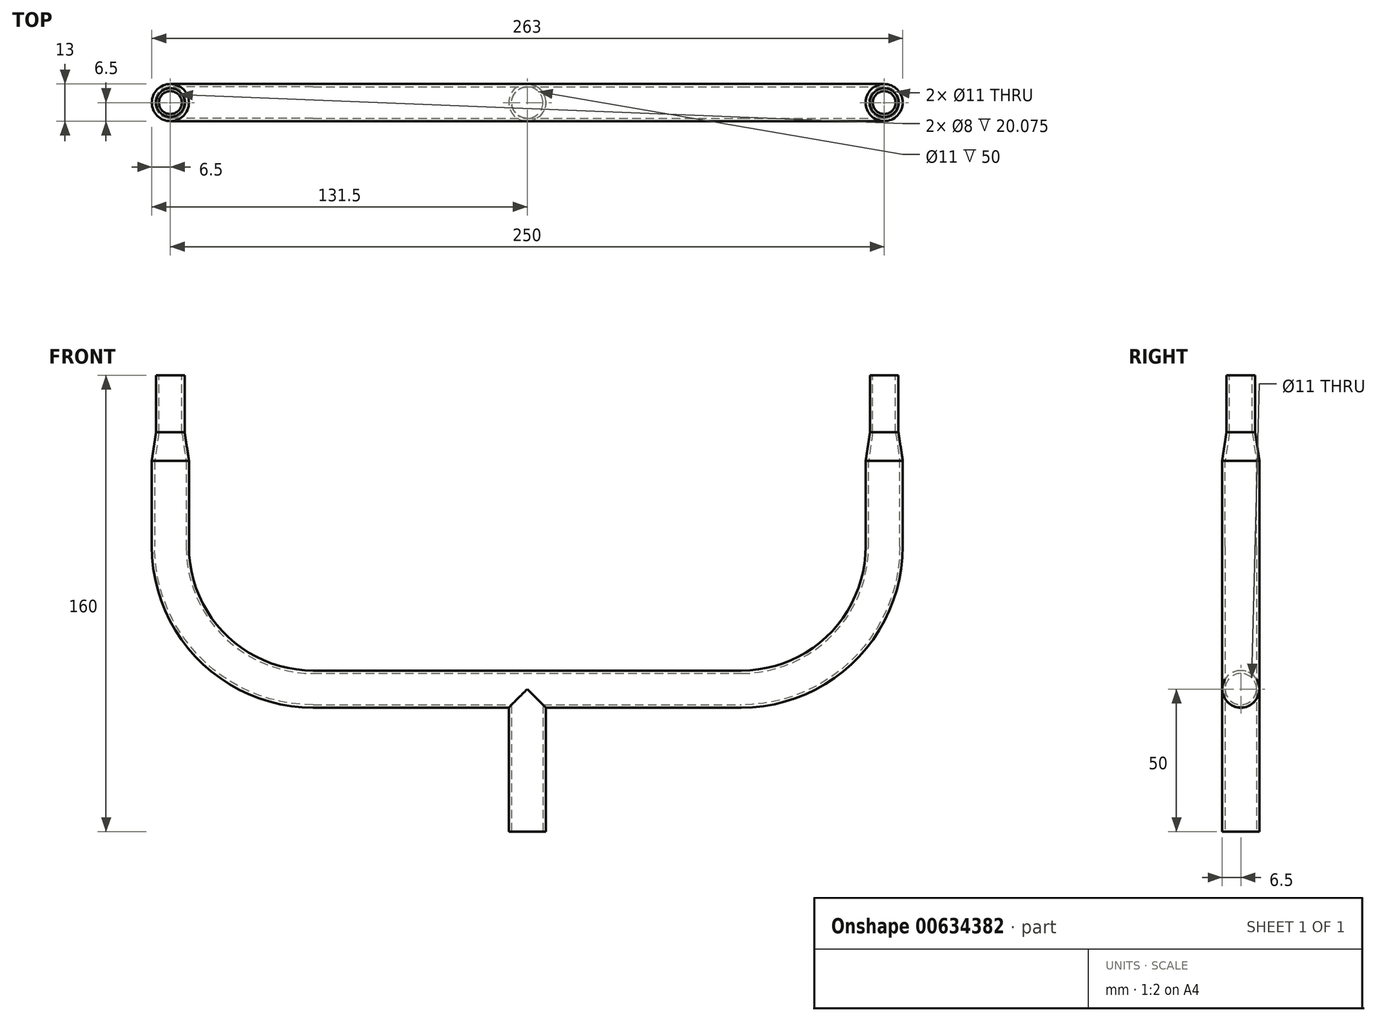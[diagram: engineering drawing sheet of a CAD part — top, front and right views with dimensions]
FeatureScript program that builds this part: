
annotation { "Feature Type Name" : "Feature", "Feature Type Description" : "" }
export const myFeature = defineFeature(function(context is Context, id is Id, definition is map)
    precondition{}
    {
        {
            var Q0;
            Q0=qCreatedBy(makeId("Front.planeOp"),FACE);
            var sketch = newSketch(context, id + "F0", { "sketchPlane" : qUnion([Q0])});
            skLineSegment(sketch, "E0", {"start": v(-75, 50) * mm, "end": v(75, 50) * mm});
            skArc(sketch, "E1", {"start": v(-75, 50) * mm, "mid": v(-110.36, 64.64) * mm, "end": v(-125, 100) * mm});
            skArc(sketch, "E2", {"start": v(75, 50) * mm, "mid": v(110.36, 64.64) * mm, "end": v(125, 100) * mm});
            skLineSegment(sketch, "E3", {"start": v(-125, 100) * mm, "end": v(-125, 120) * mm});
            skLineSegment(sketch, "E4", {"start": v(125, 100) * mm, "end": v(125, 120) * mm});
            skSolve(sketch);
        }
        {
            var Q0;
            Q0=qCreatedBy(makeId("Top.planeOp"),FACE);
            var Q1;
            Q1=sQuery(id+"F0.wireOp",VERTEX,"E3.end");
            cPlane(context, id + "F1", {"entities" : qUnion([Q0, Q1]), "cplaneType" : CPlaneType.PLANE_POINT, "offset" : 100 * mm, "width" : 150 * mm, "height" : 150 * mm});
        }
        {
            var Q0;
            Q0=qCreatedBy(id+"F1.planeOp",FACE);
            var sketch = newSketch(context, id + "F2", { "sketchPlane" : qUnion([Q0])});
            skCircle(sketch, "E5", {"center": v(-125, 0) * mm, "radius": 6.5 * mm});
            skCircle(sketch, "E6.0", {"center": v(-125, 0) * mm, "radius": 5.5 * mm});
            skSolve(sketch);
        }
        {
            var Q0;
            Q0=makeQuery(id+"F2.imprint","IMPRINT",FACE,{"disambiguationData":[TD([[makeQuery(id+"F2.imprint","IMPRINT",EDGE,{"derivedFrom":sQuery(id+"F2.wireOp",EDGE,"E5")}),1.0]])]});
            var Q1;
            Q1=qConstructionFilter(qBodyType(qCreatedBy(id+"F0",EDGE),BodyType.WIRE),ConstructionObject.NO);
            sweep(context, id + "F3", {"profiles" : qUnion([Q0]), "path" : qUnion([Q1])});
        }
        {
            var Q0;
            Q0=qCreatedBy(makeId("Top.planeOp"),FACE);
            var sketch = newSketch(context, id + "F4", { "sketchPlane" : qUnion([Q0])});
            skCircle(sketch, "E7", {"center": v(0, 0) * mm, "radius": 5.5 * mm});
            skSolve(sketch);
        }
        {
            var Q0;
            Q0=qSketchRegion(id+"F4",true);
            extrude(context, id + "F5", {"entities" : qUnion([Q0]), "operationType" : NewBodyOperationType.REMOVE, "depth" : 50 * mm});
        }
        {
            var Q0;
            Q0=qCreatedBy(makeId("Top.planeOp"),FACE);
            var sketch = newSketch(context, id + "F6", { "sketchPlane" : qUnion([Q0])});
            skCircle(sketch, "E8", {"center": v(0, 0) * mm, "radius": 6.5 * mm});
            skCircle(sketch, "E9", {"center": v(0, 0) * mm, "radius": 5.5 * mm});
            skSolve(sketch);
        }
        {
            var Q0;
            Q0=makeQuery(id+"F6.imprint","IMPRINT",FACE,{"disambiguationData":[TD([[makeQuery(id+"F6.imprint","IMPRINT",EDGE,{"derivedFrom":sQuery(id+"F6.wireOp",EDGE,"E8")}),1.0]])]});
            extrude(context, id + "F7", {"entities" : qUnion([Q0]), "operationType" : NewBodyOperationType.ADD, "endBound" : BoundingType.UP_TO_NEXT, "depth" : 25 * mm});
        }
        {
            var Q0;
            Q0=qCreatedBy(makeId("Front.planeOp"),FACE);
            var sketch = newSketch(context, id + "F8", { "sketchPlane" : qUnion([Q0])});
            skLineSegment(sketch, "E10", {"start": v(-125, 160) * mm, "end": v(-125, 120) * mm, "construction": true});
            skLineSegment(sketch, "E11", {"start": v(-118.5, 120) * mm, "end": v(-118.5, 130) * mm});
            skLineSegment(sketch, "E12", {"start": v(-118.5, 130) * mm, "end": v(-120, 140) * mm});
            skLineSegment(sketch, "E13", {"start": v(-120, 140) * mm, "end": v(-120, 160) * mm});
            skLineSegment(sketch, "E14.0", {"start": v(-121, 139.93) * mm, "end": v(-121, 160) * mm});
            skLineSegment(sketch, "E14.1", {"start": v(-119.5, 129.93) * mm, "end": v(-121, 139.93) * mm});
            skLineSegment(sketch, "E14.2", {"start": v(-119.5, 120) * mm, "end": v(-119.5, 129.93) * mm});
            skLineSegment(sketch, "E15", {"start": v(-118.5, 120) * mm, "end": v(-119.5, 120) * mm});
            skLineSegment(sketch, "E16", {"start": v(-121, 160) * mm, "end": v(-120, 160) * mm});
            skSolve(sketch);
        }
        {
            var Q0;
            Q0=makeQuery(id+"F8.imprint","IMPRINT",FACE,{"disambiguationData":[TD([[makeQuery(id+"F8.imprint","IMPRINT",EDGE,{"derivedFrom":sQuery(id+"F8.wireOp",EDGE,"E11")}),1.0]])]});
            var Q1;
            Q1=sQuery(id+"F8.wireOp",EDGE,"E10");
            revolve(context, id + "F9", {"operationType" : NewBodyOperationType.ADD, "entities" : qUnion([Q0]), "axis" : qUnion([Q1]), "revolveType" : RevolveType.FULL});
        }
        {
            var Q0;
            Q0=qCreatedBy(makeId("Front.planeOp"),FACE);
            var sketch = newSketch(context, id + "F10", { "sketchPlane" : qUnion([Q0])});
            skLineSegment(sketch, "E17", {"start": v(125, 160) * mm, "end": v(125, 120) * mm, "construction": true});
            skLineSegment(sketch, "E18", {"start": v(131.5, 120) * mm, "end": v(131.5, 130) * mm});
            skLineSegment(sketch, "E19", {"start": v(131.5, 130) * mm, "end": v(130, 140) * mm});
            skLineSegment(sketch, "E20", {"start": v(130, 140) * mm, "end": v(130, 160) * mm});
            skLineSegment(sketch, "E21.0", {"start": v(129, 139.93) * mm, "end": v(129, 160) * mm});
            skLineSegment(sketch, "E21.1", {"start": v(130.5, 129.93) * mm, "end": v(129, 139.93) * mm});
            skLineSegment(sketch, "E21.2", {"start": v(130.5, 120) * mm, "end": v(130.5, 129.93) * mm});
            skLineSegment(sketch, "E22", {"start": v(131.5, 120) * mm, "end": v(130.5, 120) * mm});
            skLineSegment(sketch, "E23", {"start": v(129, 160) * mm, "end": v(130, 160) * mm});
            skSolve(sketch);
        }
        {
            var Q0;
            Q0=makeQuery(id+"F10.imprint","IMPRINT",FACE,{"disambiguationData":[TD([[makeQuery(id+"F10.imprint","IMPRINT",EDGE,{"derivedFrom":sQuery(id+"F10.wireOp",EDGE,"E18")}),1.0]])]});
            var Q1;
            Q1=sQuery(id+"F10.wireOp",EDGE,"E17");
            revolve(context, id + "F11", {"operationType" : NewBodyOperationType.ADD, "entities" : qUnion([Q0]), "axis" : qUnion([Q1]), "revolveType" : RevolveType.FULL});
        }
    });
